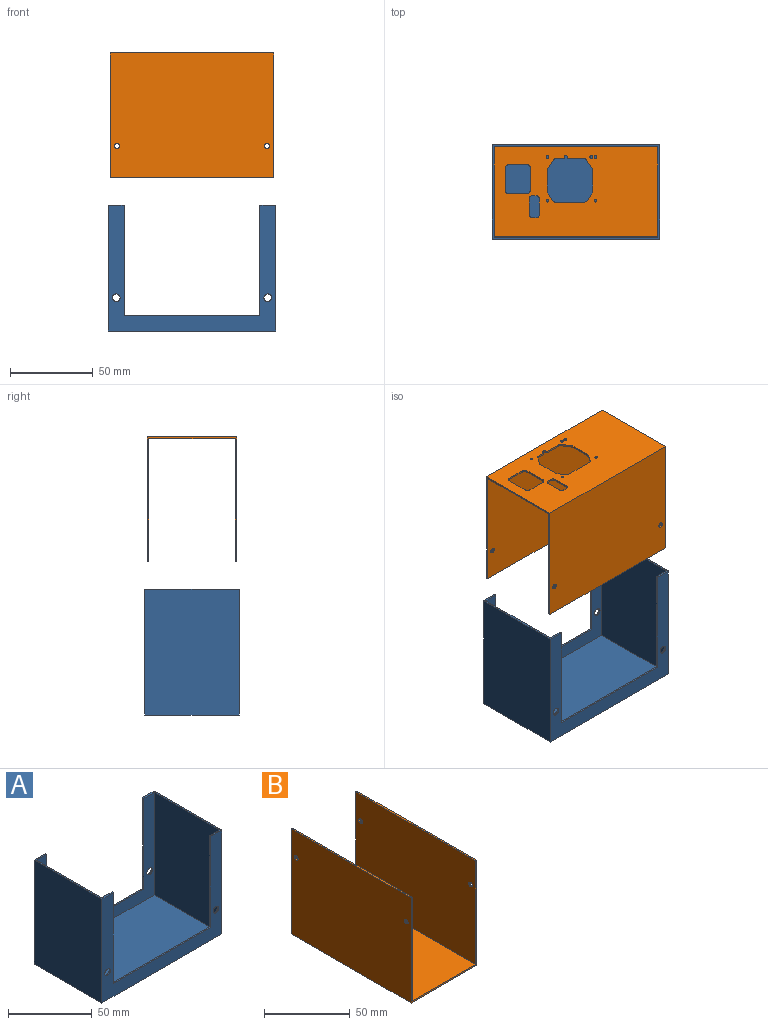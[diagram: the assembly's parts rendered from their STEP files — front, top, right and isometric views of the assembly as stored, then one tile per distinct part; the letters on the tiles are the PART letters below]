
ASSEMBLY  parts=2 mates=1
PART A: 22 faces, bbox 101x57x76 mm
  f0: plane 57x9.5mm, normal (0,0,1), area 74mm2, adj f1,f7,f10,f11,f12,f13,f14,f17
  f1: plane 76x57mm, normal (-1,0,0), area 4332mm2, adj f0,f2,f11,f17
  f2: plane 101x57mm, normal (0,0,-1), area 5757mm2, adj f1,f3,f11,f17
  f3: plane 76x57mm, normal (1,0,0), area 4332mm2, adj f2,f4,f11,f17
  f4: plane 57x9.5mm, normal (0,0,1), area 74mm2, adj f3,f5,f8,f11,f12,f13,f16,f17
  f5: plane 75x55mm, normal (-1,0,0), area 4125mm2, adj f4,f6,f12,f13
  f6: plane 99x55mm, normal (0,0,1), area 5445mm2, adj f5,f7,f12,f13
  f7: plane 75x55mm, normal (1,0,0), area 4125mm2, adj f0,f6,f12,f13
  f8: plane 66.5x1mm, normal (-1,0,0), area 66.5mm2, adj f4,f9,f11,f12
  f9: plane 82x1mm, normal (0,0,1), area 82mm2, adj f8,f10,f11,f12
  f10: plane 66.5x1mm, normal (1,0,0), area 66.5mm2, adj f0,f9,f11,f12
  f11: plane 101x76mm, normal (0,-1,0), area 2189.8mm2, adj f0,f1,f2,f3,f4,f8,f9,f10
  f12: plane 99x75mm, normal (0,1,0), area 1938.8mm2, adj f0,f4,f5,f6,f7,f8,f9,f10
  f13: plane 99x75mm, normal (0,-1,0), area 1938.8mm2, adj f0,f4,f5,f6,f7,f14,f15,f16
  f14: plane 66.5x1mm, normal (1,0,0), area 66.5mm2, adj f0,f13,f15,f17
  f15: plane 82x1mm, normal (0,0,1), area 82mm2, adj f13,f14,f16,f17
  f16: plane 66.5x1mm, normal (-1,0,0), area 66.5mm2, adj f4,f13,f15,f17
  f17: plane 101x76mm, normal (0,1,0), area 2189.8mm2, adj f0,f1,f2,f3,f4,f14,f15,f16
  f18: cylinder r=2.3mm len=4.6mm, axis (0,1,0), area 14.5mm2, adj f13,f17
  f19: cylinder r=2.3mm len=4.6mm, axis (0,1,0), area 14.5mm2, adj f13,f17
  f20: cylinder r=2.3mm len=4.6mm, axis (0,1,0), area 14.5mm2, adj f11,f12
  f21: cylinder r=2.3mm len=4.6mm, axis (0,1,0), area 14.5mm2, adj f11,f12
PART B: 57 faces, bbox 54x98.7x75 mm
  f0: plane 98.7x1mm, normal (0,0,1), area 98.7mm2, adj f1,f7,f8,f9
  f1: plane 98.7x75mm, normal (-1,0,0), area 7388.4mm2, adj f0,f2,f8,f9,f10,f11
  f2: plane 98.7x54mm, normal (0,0,-1), area 4309.1mm2, adj f1,f3,f8,f9,f14,f15,f16,f17
  f3: plane 98.7x75mm, normal (1,0,0), area 7388.4mm2, adj f2,f4,f8,f9,f12,f13
  f4: plane 98.7x1mm, normal (0,0,1), area 98.7mm2, adj f3,f5,f8,f9
  f5: plane 98.7x74mm, normal (-1,0,0), area 7289.7mm2, adj f4,f6,f8,f9,f12,f13
  f6: plane 98.7x52mm, normal (0,0,1), area 4111.7mm2, adj f5,f7,f8,f9,f14,f15,f16,f17
  f7: plane 98.7x74mm, normal (1,0,0), area 7289.7mm2, adj f0,f6,f8,f9,f10,f11
  f8: plane 75x54mm, normal (0,-1,0), area 202mm2, adj f0,f1,f2,f3,f4,f5,f6,f7
  f9: plane 75x54mm, normal (0,1,0), area 202mm2, adj f0,f1,f2,f3,f4,f5,f6,f7
  f10: cylinder r=1.5mm len=3mm, axis (1,0,0), area 9.4mm2, adj f1,f7
  f11: cylinder r=1.5mm len=3mm, axis (1,0,0), area 9.4mm2, adj f1,f7
  f12: cylinder r=1.5mm len=3mm, axis (1,0,0), area 9.4mm2, adj f3,f5
  f13: cylinder r=1.5mm len=3mm, axis (1,0,0), area 9.4mm2, adj f3,f5
  f14: plane 4.45x1mm, normal (1,0,0), area 4.4mm2, adj f2,f6,f33,f55
  f15: plane 1x0.5mm, normal (0,-1,0), area 0.5mm2, adj f2,f6,f16,f55
  f16: cylinder r=0.9mm len=1.8mm, axis (0,0,1), area 2.8mm2, adj f2,f6,f15,f17
  f17: plane 1x0.5mm, normal (0,1,0), area 0.5mm2, adj f2,f6,f16,f56
  f18: plane 9.45x1mm, normal (1,0,0), area 9.4mm2, adj f2,f6,f19,f56
  f19: cylinder r=2mm len=1.69mm, axis (0,0,1), area 2mm2, adj f2,f6,f18,f20
  f20: plane 5.33x3.4mm, normal (0.54,0.84,0), area 6.3mm2, adj f2,f6,f19,f21
  f21: cylinder r=2mm len=1.08mm, axis (0,0,1), area 1.1mm2, adj f2,f6,f20,f22
  f22: plane 12.38x1mm, normal (0,1,0), area 12.4mm2, adj f2,f6,f21,f23
  f23: cylinder r=2mm len=1.08mm, axis (0,0,1), area 1.1mm2, adj f2,f6,f22,f24
  f24: plane 4.59x2.93mm, normal (-0.54,0.84,0), area 5.5mm2, adj f2,f6,f23,f25
  f25: cylinder r=2mm len=1.69mm, axis (0,0,1), area 2mm2, adj f2,f6,f24,f26
  f26: plane 17.63x1mm, normal (-1,0,0), area 17.6mm2, adj f2,f6,f25,f27
  f27: cylinder r=2mm len=1.69mm, axis (0,0,1), area 2mm2, adj f2,f6,f26,f28
  f28: plane 4.59x2.93mm, normal (-0.54,-0.84,0), area 5.5mm2, adj f2,f6,f27,f29
  f29: cylinder r=2mm len=1.08mm, axis (0,0,1), area 1.1mm2, adj f2,f6,f28,f30
  f30: plane 12.38x1mm, normal (0,-1,0), area 12.4mm2, adj f2,f6,f29,f31
  f31: cylinder r=2mm len=1.08mm, axis (0,0,1), area 1.1mm2, adj f2,f6,f30,f32
  f32: plane 5.33x3.4mm, normal (0.54,-0.84,0), area 6.3mm2, adj f2,f6,f31,f33
  f33: cylinder r=2mm len=1.69mm, axis (0,0,1), area 2mm2, adj f2,f6,f14,f32
  f34: cylinder r=0.9mm len=1.8mm, axis (0,0,1), area 5.7mm2, adj f2,f6
  f35: cylinder r=0.8mm len=1.6mm, axis (0,0,1), area 5mm2, adj f2,f6
  f36: cylinder r=0.8mm len=1.6mm, axis (0,0,1), area 5mm2, adj f2,f6
  f37: cylinder r=0.8mm len=1.6mm, axis (0,0,1), area 5mm2, adj f2,f6
  f38: cylinder r=0.8mm len=1.6mm, axis (0,0,1), area 5mm2, adj f2,f6
  f39: plane 9.5x1mm, normal (0,-1,0), area 9.5mm2, adj f2,f6,f40,f46
  f40: cylinder r=2mm len=2mm, axis (0,0,1), area 3.1mm2, adj f2,f6,f39,f41
  f41: plane 2x1mm, normal (1,0,0), area 2mm2, adj f2,f6,f40,f42
  f42: cylinder r=2mm len=2mm, axis (0,0,1), area 3.1mm2, adj f2,f6,f41,f43
  f43: plane 9.5x1mm, normal (0,1,0), area 9.5mm2, adj f2,f6,f42,f44
  f44: cylinder r=2mm len=2mm, axis (0,0,1), area 3.1mm2, adj f2,f6,f43,f45
  f45: plane 2x1mm, normal (-1,0,0), area 2mm2, adj f2,f6,f44,f46
  f46: cylinder r=2mm len=2mm, axis (0,0,1), area 3.1mm2, adj f2,f6,f39,f45
  f47: plane 13.5x1mm, normal (0,-1,0), area 13.5mm2, adj f2,f6,f48,f54
  f48: cylinder r=2mm len=2mm, axis (0,0,1), area 3.1mm2, adj f2,f6,f47,f49
  f49: plane 11x1mm, normal (1,0,0), area 11mm2, adj f2,f6,f48,f50
  f50: cylinder r=2mm len=2mm, axis (0,0,1), area 3.1mm2, adj f2,f6,f49,f51
  f51: plane 13.5x1mm, normal (0,1,0), area 13.5mm2, adj f2,f6,f50,f52
  f52: cylinder r=2mm len=2mm, axis (0,0,1), area 3.1mm2, adj f2,f6,f51,f53
  f53: plane 11x1mm, normal (-1,0,0), area 11mm2, adj f2,f6,f52,f54
  f54: cylinder r=2mm len=2mm, axis (0,0,1), area 3.1mm2, adj f2,f6,f47,f53
  f55: cylinder r=0.5mm len=1mm, axis (0,0,-1), area 0.8mm2, adj f2,f6,f14,f15
  f56: cylinder r=0.5mm len=1mm, axis (0,0,-1), area 0.8mm2, adj f2,f6,f17,f18
PLACE A t=(-115.51,-3.76,-33.66)mm
PLACE B rot(axis=(-0.71,0.71,0),180deg) t=(-114.36,-4.26,134.24)mm
MATE slider B.f0 <-> A.f6  axis (0,0,-1) through (-65.01,-31.26,59.24)mm
